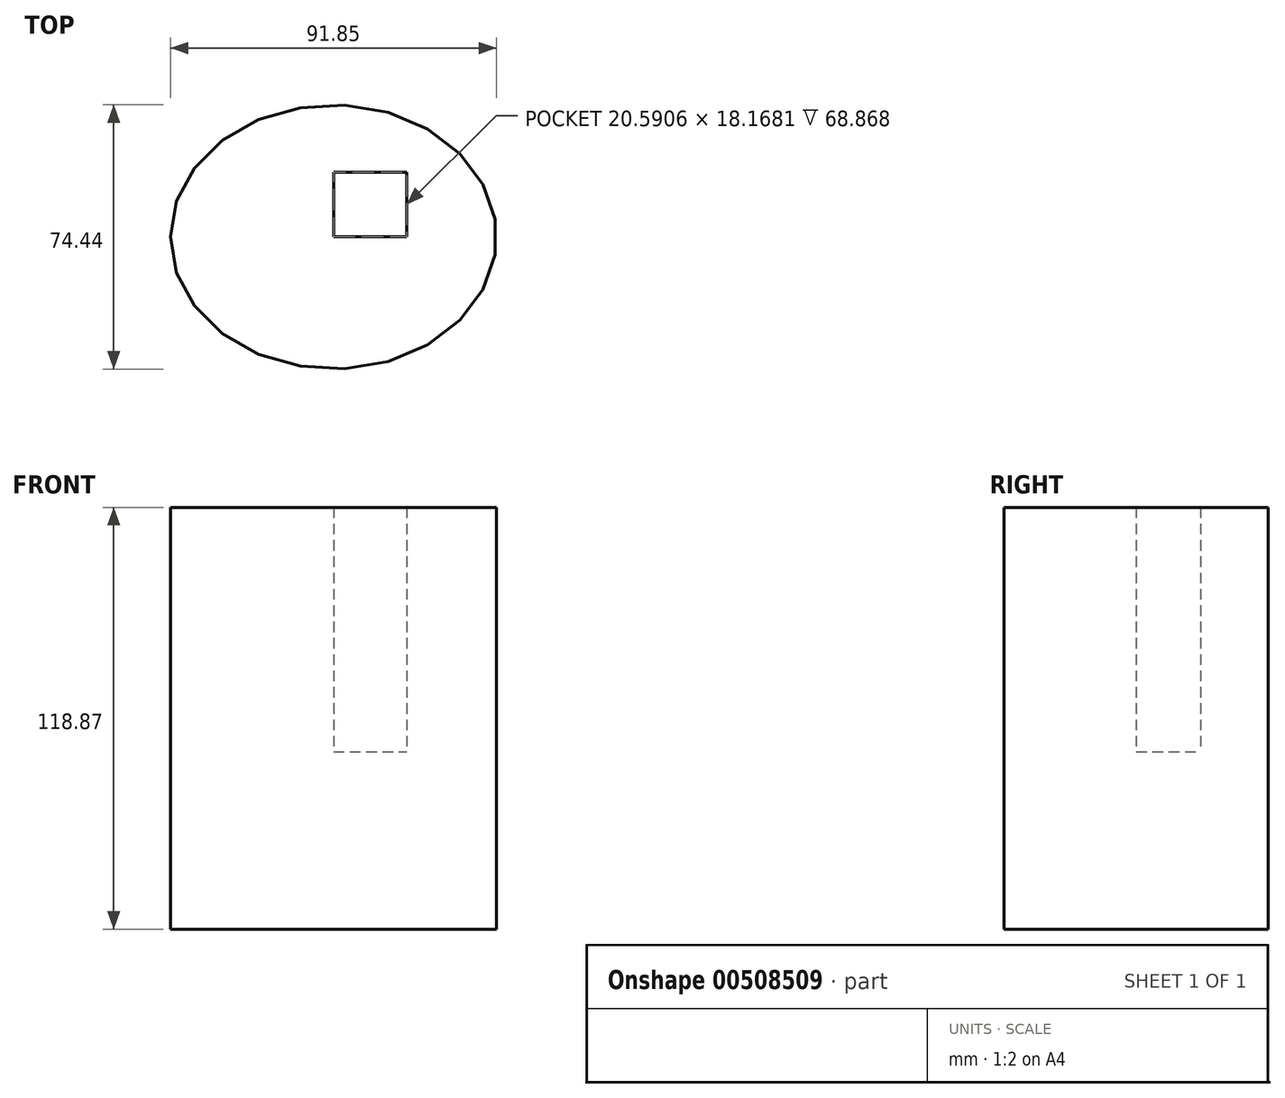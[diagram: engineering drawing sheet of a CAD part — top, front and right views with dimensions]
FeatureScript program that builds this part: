
annotation { "Feature Type Name" : "Feature", "Feature Type Description" : "" }
export const myFeature = defineFeature(function(context is Context, id is Id, definition is map)
    precondition{}
    {
        {
            var Q0;
            Q0=qCreatedBy(makeId("Top.planeOp"),FACE);
            var sketch = newSketch(context, id + "F0", { "sketchPlane" : qUnion([Q0])});
            skEllipse(sketch, "E0", {"center": v(23.52, 26.18) * mm, "majorRadius": 45.92 * mm, "minorRadius": 37.22 * mm, "majorAxis": v(-1, 0)});
            skSolve(sketch);
        }
        {
            var Q0;
            Q0 = qSketchRegion(id + "F0", true);
            extrude(context, id + "F1", {"entities" : qUnion([Q0]), "depth" : 25 * mm});
        }
        {
            var Q0;
            Q0=makeQuery(id+"F1.opExtrude","CAP_FACE",FACE,{"disambiguationData":[OSD([sQuery(id+"F0.wireOp",EDGE,"E0")])],"isStart":false});
            var sketch = newSketch(context, id + "F2", { "sketchPlane" : qUnion([Q0])});
            skLineSegment(sketch, "E1.bottom", {"start": v(23.52, 26.18) * mm, "end": v(44.11, 26.18) * mm});
            skLineSegment(sketch, "E1.top", {"start": v(23.52, 44.35) * mm, "end": v(44.11, 44.35) * mm});
            skLineSegment(sketch, "E1.left", {"start": v(23.52, 26.18) * mm, "end": v(23.52, 44.35) * mm});
            skLineSegment(sketch, "E1.right", {"start": v(44.11, 26.18) * mm, "end": v(44.11, 44.35) * mm});
            skSolve(sketch);
        }
        {
            var Q0;
            Q0 = qSketchRegion(id + "F2", true);
            extrude(context, id + "F3", {"entities" : qUnion([Q0]), "operationType" : NewBodyOperationType.ADD, "depth" : 25 * mm});
        }
        {
            var Q0;
            Q0=makeQuery(id+"F3.opExtrude","CAP_FACE",FACE,{"disambiguationData":[OSD([sQuery(id+"F2.wireOp",EDGE,"E1.bottom"),sQuery(id+"F2.wireOp",EDGE,"E1.top"),sQuery(id+"F2.wireOp",EDGE,"E1.left"),sQuery(id+"F2.wireOp",EDGE,"E1.right")])],"isStart":false});
            var sketch = newSketch(context, id + "F4", { "sketchPlane" : qUnion([Q0])});
            skCircle(sketch, "E2", {"center": v(33.63, 35.2) * mm, "radius": 5.1 * mm});
            skSolve(sketch);
        }
        {
            var Q0;
            Q0 = qSketchRegion(id + "F4", true);
            var Q1;
            Q1=sQuery(id+"F4.wireOp",EDGE,"E2");
            extrude(context, id + "F5", {"entities" : qUnion([Q0]), "bodyType" : ToolBodyType.SURFACE, "surfaceEntities" : qUnion([Q1]), "depth" : 6.2 * mm});
        }
        {
            var Q0;
            Q0=makeQuery(id+"F1.opExtrude","CAP_FACE",FACE,{"disambiguationData":[OSD([sQuery(id+"F0.wireOp",EDGE,"E0")])],"isStart":false});
            extrude(context, id + "F6", {"entities" : qUnion([Q0]), "operationType" : NewBodyOperationType.ADD, "depth" : 93.87 * mm});
        }
    });
